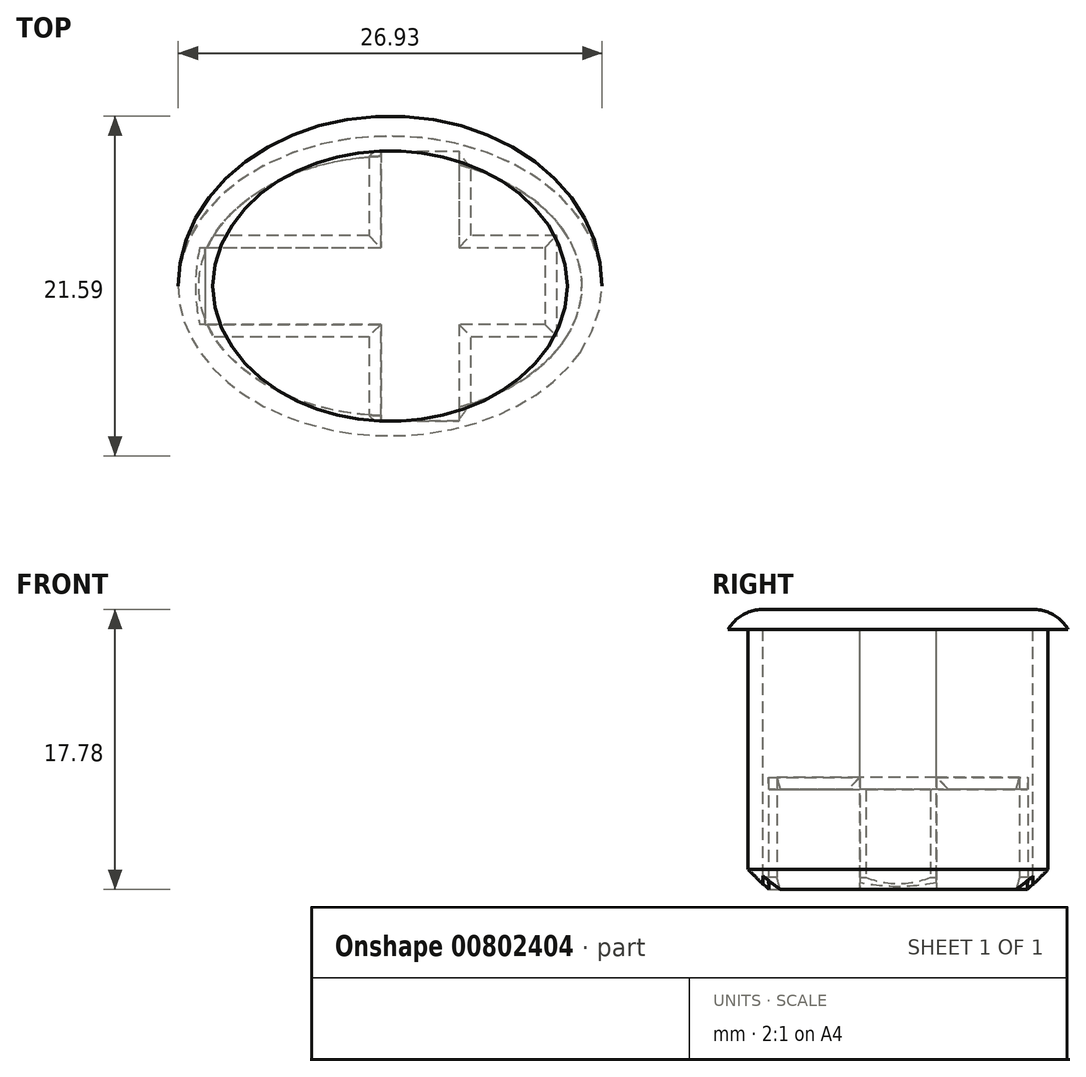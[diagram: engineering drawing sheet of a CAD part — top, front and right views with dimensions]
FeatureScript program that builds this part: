
annotation { "Feature Type Name" : "Feature", "Feature Type Description" : "" }
export const myFeature = defineFeature(function(context is Context, id is Id, definition is map)
    precondition{}
    {
        {
            var Q0;
            Q0=qCreatedBy(makeId("Top.planeOp"),FACE);
            var sketch = newSketch(context, id + "F0", { "sketchPlane" : qUnion([Q0])});
            skLineSegment(sketch, "E0.bottom", {"start": v(-13.65, 2.44) * mm, "end": v(7.94, 2.44) * mm});
            skLineSegment(sketch, "E0.top", {"start": v(-13.65, -2.44) * mm, "end": v(7.94, -2.44) * mm});
            skLineSegment(sketch, "E0.left", {"start": v(-13.65, 2.44) * mm, "end": v(-13.65, -2.44) * mm});
            skLineSegment(sketch, "E0.right", {"start": v(7.94, 2.44) * mm, "end": v(7.94, -2.44) * mm});
            skPoint(sketch, "E0.middle", {"position": v(0, 0) * mm});
            skLineSegment(sketch, "E1.bottom", {"start": v(-2.48, 8.57) * mm, "end": v(2.48, 8.57) * mm});
            skLineSegment(sketch, "E1.top", {"start": v(-2.48, -8.57) * mm, "end": v(2.48, -8.57) * mm});
            skLineSegment(sketch, "E1.left", {"start": v(-2.48, 8.57) * mm, "end": v(-2.48, -8.57) * mm});
            skLineSegment(sketch, "E1.right", {"start": v(2.48, 8.57) * mm, "end": v(2.48, -8.57) * mm});
            skEllipse(sketch, "E2", {"center": v(-1.89, 0) * mm, "majorRadius": 13.46 * mm, "minorRadius": 9.53 * mm, "majorAxis": v(-1, 0)});
            skPoint(sketch, "E3", {"position": v(-2.48, 0) * mm});
            skSolve(sketch);
        }
        {
            var Q0;
            {var subQ8=sQuery(id+"F0.wireOp",EDGE,"E0.left");Q0=makeQuery(id+"F0.imprint","IMPRINT",FACE,{"disambiguationData":[TD([[makeQuery(id+"F0.imprint","IMPRINT",EDGE,{"derivedFrom":subQ8}),-1.0]])]});}
            extrude(context, id + "F1", {"entities" : qUnion([Q0]), "oppositeDirection" : true, "depth" : 16.5 * mm, "offsetDistance" : 25.4 * mm});
        }
        {
            var Q0;
            Q0=makeQuery(id+"F1.opExtrude","CAP_FACE",FACE,{"disambiguationData":[OSD([sQuery(id+"F0.wireOp",EDGE,"E0.bottom"),sQuery(id+"F0.wireOp",EDGE,"E0.top"),sQuery(id+"F0.wireOp",EDGE,"E0.left"),sQuery(id+"F0.wireOp",EDGE,"E0.right"),sQuery(id+"F0.wireOp",EDGE,"E1.bottom"),sQuery(id+"F0.wireOp",EDGE,"E1.top"),sQuery(id+"F0.wireOp",EDGE,"E1.left"),sQuery(id+"F0.wireOp",EDGE,"E1.right"),sQuery(id+"F0.wireOp",EDGE,"E2")])],"isStart":true});
            var sketch = newSketch(context, id + "F2", { "sketchPlane" : qUnion([Q0])});
            skEllipse(sketch, "E4.0", {"center": v(-1.89, 0) * mm, "majorRadius": 13.46 * mm, "minorRadius": 10.8 * mm, "majorAxis": v(-1, 0)});
            skSolve(sketch);
        }
        {
            var Q0;
            Q0 = qSketchRegion(id + "F2", true);
            extrude(context, id + "F3", {"entities" : qUnion([Q0]), "operationType" : NewBodyOperationType.ADD, "depth" : 1.27 * mm, "offsetDistance" : 25.4 * mm});
        }
        {
            var Q0;
            Q0=makeQuery(id+"F3.opExtrude","CAP_EDGE",EDGE,{"disambiguationData":[OSD([sQuery(id+"F2.wireOp",EDGE,"E4.0")])],"isStart":false});
            fillet(context, id + "F4", {"entities" : qUnion([Q0]), "radius" : 2.54 * mm, "tangentPropagation" : true, "allowEdgeOverflow" : false});
        }
        {
            var Q0;
            Q0=makeQuery(id+"F1.opExtrude","CAP_EDGE",EDGE,{"disambiguationData":[OSD([sQuery(id+"F0.wireOp",EDGE,"E2")])],"isStart":false});
            chamfer(context, id + "F5", {"entities" : qUnion([Q0]), "width" : 1.27 * mm, "tangentPropagation" : true});
        }
        {
            var Q0;
            Q0=makeQuery(id+"F1.opExtrude","CAP_EDGE",EDGE,{"disambiguationData":[OSD([sQuery(id+"F0.wireOp",EDGE,"E0.left")])],"isStart":false});
            var Q1;
            {var subQ0=sQuery(id+"F0.wireOp",EDGE,"E1.left");Q1=makeQuery(id+"F1.opExtrude","CAP_EDGE",EDGE,{"disambiguationData":[OSD([subQ0]),TDD([makeQuery(id+"F0.imprint","IMPRINT",EDGE,{"disambiguationData":[TD([[makeQuery(id+"F0.imprint","INTERSECT",VERTEX,{"derivedFrom":[sQuery(id+"F0.wireOp",EDGE,"E1.bottom"),subQ0]}),-1.0]])],"derivedFrom":subQ0})])],"isStart":false});}
            var Q2;
            {var subQ0=sQuery(id+"F0.wireOp",EDGE,"E1.right");Q2=makeQuery(id+"F1.opExtrude","CAP_EDGE",EDGE,{"disambiguationData":[OSD([subQ0]),TDD([makeQuery(id+"F0.imprint","IMPRINT",EDGE,{"disambiguationData":[TD([[makeQuery(id+"F0.imprint","INTERSECT",VERTEX,{"derivedFrom":[sQuery(id+"F0.wireOp",EDGE,"E1.bottom"),subQ0]}),-1.0]])],"derivedFrom":subQ0})])],"isStart":false});}
            var Q3;
            Q3=makeQuery(id+"F1.opExtrude","CAP_EDGE",EDGE,{"disambiguationData":[OSD([sQuery(id+"F0.wireOp",EDGE,"E1.bottom")])],"isStart":false});
            var Q4;
            {var subQ0=sQuery(id+"F0.wireOp",EDGE,"E0.bottom");Q4=makeQuery(id+"F1.opExtrude","CAP_EDGE",EDGE,{"disambiguationData":[OSD([subQ0]),TDD([makeQuery(id+"F0.imprint","IMPRINT",EDGE,{"disambiguationData":[TD([[makeQuery(id+"F0.imprint","INTERSECT",VERTEX,{"derivedFrom":[subQ0,sQuery(id+"F0.wireOp",EDGE,"E0.right")]}),1.0]])],"derivedFrom":subQ0})])],"isStart":false});}
            var Q5;
            Q5=makeQuery(id+"F1.opExtrude","CAP_EDGE",EDGE,{"disambiguationData":[OSD([sQuery(id+"F0.wireOp",EDGE,"E0.right")])],"isStart":false});
            var Q6;
            {var subQ0=sQuery(id+"F0.wireOp",EDGE,"E0.top");Q6=makeQuery(id+"F1.opExtrude","CAP_EDGE",EDGE,{"disambiguationData":[OSD([subQ0]),TDD([makeQuery(id+"F0.imprint","IMPRINT",EDGE,{"disambiguationData":[TD([[makeQuery(id+"F0.imprint","INTERSECT",VERTEX,{"derivedFrom":[subQ0,sQuery(id+"F0.wireOp",EDGE,"E0.right")]}),1.0]])],"derivedFrom":subQ0})])],"isStart":false});}
            var Q7;
            {var subQ0=sQuery(id+"F0.wireOp",EDGE,"E1.right");Q7=makeQuery(id+"F1.opExtrude","CAP_EDGE",EDGE,{"disambiguationData":[OSD([subQ0]),TDD([makeQuery(id+"F0.imprint","IMPRINT",EDGE,{"disambiguationData":[TD([[makeQuery(id+"F0.imprint","INTERSECT",VERTEX,{"derivedFrom":[sQuery(id+"F0.wireOp",EDGE,"E1.top"),subQ0]}),1.0]])],"derivedFrom":subQ0})])],"isStart":false});}
            var Q8;
            Q8=makeQuery(id+"F1.opExtrude","CAP_EDGE",EDGE,{"disambiguationData":[OSD([sQuery(id+"F0.wireOp",EDGE,"E1.top")])],"isStart":false});
            var Q9;
            {var subQ0=sQuery(id+"F0.wireOp",EDGE,"E1.left");Q9=makeQuery(id+"F1.opExtrude","CAP_EDGE",EDGE,{"disambiguationData":[OSD([subQ0]),TDD([makeQuery(id+"F0.imprint","IMPRINT",EDGE,{"disambiguationData":[TD([[makeQuery(id+"F0.imprint","INTERSECT",VERTEX,{"derivedFrom":[sQuery(id+"F0.wireOp",EDGE,"E1.top"),subQ0]}),1.0]])],"derivedFrom":subQ0})])],"isStart":false});}
            chamfer(context, id + "F6", {"entities" : qUnion([Q0, Q1, Q2, Q3, Q4, Q5, Q6, Q7, Q8, Q9]), "width" : 0.76 * mm, "tangentPropagation" : true});
        }
        {
            var Q0;
            Q0=makeQuery(id+"F5.opChamfer","SPLIT",FACE,{"disambiguationData":[OD(2.0)],"derivedFrom":makeQuery(id+"F1.opExtrude","CAP_FACE",FACE,{"disambiguationData":[OSD([sQuery(id+"F0.wireOp",EDGE,"E0.bottom"),sQuery(id+"F0.wireOp",EDGE,"E0.top"),sQuery(id+"F0.wireOp",EDGE,"E0.left"),sQuery(id+"F0.wireOp",EDGE,"E0.right"),sQuery(id+"F0.wireOp",EDGE,"E1.bottom"),sQuery(id+"F0.wireOp",EDGE,"E1.top"),sQuery(id+"F0.wireOp",EDGE,"E1.left"),sQuery(id+"F0.wireOp",EDGE,"E1.right"),sQuery(id+"F0.wireOp",EDGE,"E2")])],"isStart":false})});
            var sketch = newSketch(context, id + "F7", { "sketchPlane" : qUnion([Q0])});
            skEllipse(sketch, "E5", {"center": v(-1.88, 0) * mm, "majorRadius": 12.16 * mm, "minorRadius": 8.25 * mm, "majorAxis": v(-1, 0)});
            skSolve(sketch);
        }
        {
            var Q0;
            Q0 = qSketchRegion(id + "F7", true);
            extrude(context, id + "F8", {"entities" : qUnion([Q0]), "operationType" : NewBodyOperationType.REMOVE, "oppositeDirection" : true, "depth" : 6.35 * mm, "offsetDistance" : 25.4 * mm});
        }
        {
            var Q0;
            {var subQ0=sQuery(id+"F0.wireOp",EDGE,"E0.top");Q0=makeQuery(id+"F8.boolean.opBoolean","INTERSECT",EDGE,{"derivedFrom":[makeQuery(id+"F1.opExtrude","SWEPT_FACE",FACE,{"disambiguationData":[OSD([subQ0]),TDD([makeQuery(id+"F0.imprint","IMPRINT",EDGE,{"disambiguationData":[TD([[makeQuery(id+"F0.imprint","INTERSECT",VERTEX,{"derivedFrom":[subQ0,sQuery(id+"F0.wireOp",EDGE,"E0.left")]}),-1.0]])],"derivedFrom":subQ0})])]}),makeQuery(id+"F8.opExtrude","CAP_FACE",FACE,{"disambiguationData":[OSD([sQuery(id+"F7.wireOp",EDGE,"E5")])],"isStart":false})]});}
            var Q1;
            {var subQ0=sQuery(id+"F0.wireOp",EDGE,"E1.left");Q1=makeQuery(id+"F8.boolean.opBoolean","INTERSECT",EDGE,{"derivedFrom":[makeQuery(id+"F1.opExtrude","SWEPT_FACE",FACE,{"disambiguationData":[OSD([subQ0]),TDD([makeQuery(id+"F0.imprint","IMPRINT",EDGE,{"disambiguationData":[TD([[makeQuery(id+"F0.imprint","INTERSECT",VERTEX,{"derivedFrom":[sQuery(id+"F0.wireOp",EDGE,"E1.top"),subQ0]}),1.0]])],"derivedFrom":subQ0})])]}),makeQuery(id+"F8.opExtrude","CAP_FACE",FACE,{"disambiguationData":[OSD([sQuery(id+"F7.wireOp",EDGE,"E5")])],"isStart":false})]});}
            var Q2;
            {var subQ0=sQuery(id+"F0.wireOp",EDGE,"E1.right");Q2=makeQuery(id+"F8.boolean.opBoolean","INTERSECT",EDGE,{"derivedFrom":[makeQuery(id+"F1.opExtrude","SWEPT_FACE",FACE,{"disambiguationData":[OSD([subQ0]),TDD([makeQuery(id+"F0.imprint","IMPRINT",EDGE,{"disambiguationData":[TD([[makeQuery(id+"F0.imprint","INTERSECT",VERTEX,{"derivedFrom":[sQuery(id+"F0.wireOp",EDGE,"E1.top"),subQ0]}),1.0]])],"derivedFrom":subQ0})])]}),makeQuery(id+"F8.opExtrude","CAP_FACE",FACE,{"disambiguationData":[OSD([sQuery(id+"F7.wireOp",EDGE,"E5")])],"isStart":false})]});}
            var Q3;
            {var subQ0=sQuery(id+"F0.wireOp",EDGE,"E0.top");Q3=makeQuery(id+"F8.boolean.opBoolean","INTERSECT",EDGE,{"derivedFrom":[makeQuery(id+"F1.opExtrude","SWEPT_FACE",FACE,{"disambiguationData":[OSD([subQ0]),TDD([makeQuery(id+"F0.imprint","IMPRINT",EDGE,{"disambiguationData":[TD([[makeQuery(id+"F0.imprint","INTERSECT",VERTEX,{"derivedFrom":[subQ0,sQuery(id+"F0.wireOp",EDGE,"E0.right")]}),1.0]])],"derivedFrom":subQ0})])]}),makeQuery(id+"F8.opExtrude","CAP_FACE",FACE,{"disambiguationData":[OSD([sQuery(id+"F7.wireOp",EDGE,"E5")])],"isStart":false})]});}
            var Q4;
            Q4=makeQuery(id+"F8.boolean.opBoolean","INTERSECT",EDGE,{"derivedFrom":[makeQuery(id+"F1.opExtrude","SWEPT_FACE",FACE,{"disambiguationData":[OSD([sQuery(id+"F0.wireOp",EDGE,"E0.right")])]}),makeQuery(id+"F8.opExtrude","CAP_FACE",FACE,{"disambiguationData":[OSD([sQuery(id+"F7.wireOp",EDGE,"E5")])],"isStart":false})]});
            var Q5;
            {var subQ0=sQuery(id+"F0.wireOp",EDGE,"E0.bottom");Q5=makeQuery(id+"F8.boolean.opBoolean","INTERSECT",EDGE,{"derivedFrom":[makeQuery(id+"F1.opExtrude","SWEPT_FACE",FACE,{"disambiguationData":[OSD([subQ0]),TDD([makeQuery(id+"F0.imprint","IMPRINT",EDGE,{"disambiguationData":[TD([[makeQuery(id+"F0.imprint","INTERSECT",VERTEX,{"derivedFrom":[subQ0,sQuery(id+"F0.wireOp",EDGE,"E0.right")]}),1.0]])],"derivedFrom":subQ0})])]}),makeQuery(id+"F8.opExtrude","CAP_FACE",FACE,{"disambiguationData":[OSD([sQuery(id+"F7.wireOp",EDGE,"E5")])],"isStart":false})]});}
            var Q6;
            {var subQ0=sQuery(id+"F0.wireOp",EDGE,"E1.right");Q6=makeQuery(id+"F8.boolean.opBoolean","INTERSECT",EDGE,{"derivedFrom":[makeQuery(id+"F1.opExtrude","SWEPT_FACE",FACE,{"disambiguationData":[OSD([subQ0]),TDD([makeQuery(id+"F0.imprint","IMPRINT",EDGE,{"disambiguationData":[TD([[makeQuery(id+"F0.imprint","INTERSECT",VERTEX,{"derivedFrom":[sQuery(id+"F0.wireOp",EDGE,"E1.bottom"),subQ0]}),-1.0]])],"derivedFrom":subQ0})])]}),makeQuery(id+"F8.opExtrude","CAP_FACE",FACE,{"disambiguationData":[OSD([sQuery(id+"F7.wireOp",EDGE,"E5")])],"isStart":false})]});}
            var Q7;
            {var subQ0=sQuery(id+"F0.wireOp",EDGE,"E1.left");Q7=makeQuery(id+"F8.boolean.opBoolean","INTERSECT",EDGE,{"derivedFrom":[makeQuery(id+"F1.opExtrude","SWEPT_FACE",FACE,{"disambiguationData":[OSD([subQ0]),TDD([makeQuery(id+"F0.imprint","IMPRINT",EDGE,{"disambiguationData":[TD([[makeQuery(id+"F0.imprint","INTERSECT",VERTEX,{"derivedFrom":[sQuery(id+"F0.wireOp",EDGE,"E1.bottom"),subQ0]}),-1.0]])],"derivedFrom":subQ0})])]}),makeQuery(id+"F8.opExtrude","CAP_FACE",FACE,{"disambiguationData":[OSD([sQuery(id+"F7.wireOp",EDGE,"E5")])],"isStart":false})]});}
            var Q8;
            {var subQ0=sQuery(id+"F0.wireOp",EDGE,"E0.bottom");Q8=makeQuery(id+"F8.boolean.opBoolean","INTERSECT",EDGE,{"derivedFrom":[makeQuery(id+"F1.opExtrude","SWEPT_FACE",FACE,{"disambiguationData":[OSD([subQ0]),TDD([makeQuery(id+"F0.imprint","IMPRINT",EDGE,{"disambiguationData":[TD([[makeQuery(id+"F0.imprint","INTERSECT",VERTEX,{"derivedFrom":[subQ0,sQuery(id+"F0.wireOp",EDGE,"E0.left")]}),-1.0]])],"derivedFrom":subQ0})])]}),makeQuery(id+"F8.opExtrude","CAP_FACE",FACE,{"disambiguationData":[OSD([sQuery(id+"F7.wireOp",EDGE,"E5")])],"isStart":false})]});}
            chamfer(context, id + "F9", {"entities" : qUnion([Q0, Q1, Q2, Q3, Q4, Q5, Q6, Q7, Q8]), "width" : 0.76 * mm, "tangentPropagation" : true});
        }
    });
